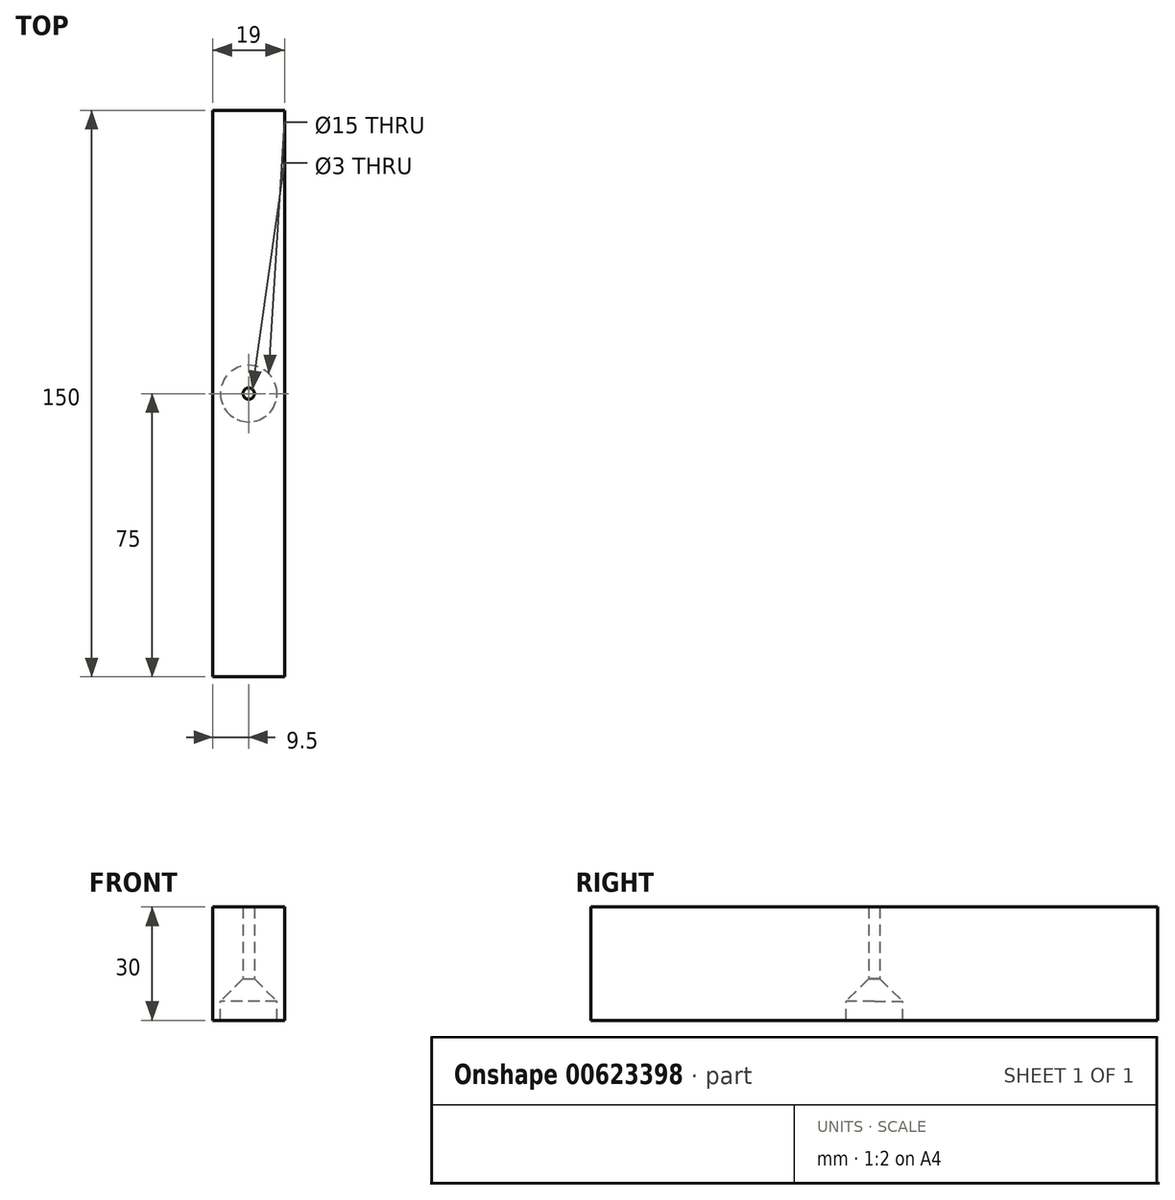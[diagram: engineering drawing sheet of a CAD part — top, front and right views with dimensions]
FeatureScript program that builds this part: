
annotation { "Feature Type Name" : "Feature", "Feature Type Description" : "" }
export const myFeature = defineFeature(function(context is Context, id is Id, definition is map)
    precondition{}
    {
        {
            var Q0;
            Q0=qCreatedBy(makeId("Top.planeOp"),FACE);
            var sketch = newSketch(context, id + "F0", { "sketchPlane" : qUnion([Q0])});
            skLineSegment(sketch, "E0", {"start": v(-50, 0) * mm, "end": v(50, 0) * mm, "construction": true});
            skLineSegment(sketch, "E1", {"start": v(0, 50) * mm, "end": v(0, -50) * mm, "construction": true});
            skSolve(sketch);
        }
        {
            var Q0;
            Q0=qCreatedBy(makeId("Front.planeOp"),FACE);
            var sketch = newSketch(context, id + "F1", { "sketchPlane" : qUnion([Q0])});
            skLineSegment(sketch, "E2.bottom", {"start": v(0, -15) * mm, "end": v(19, -15) * mm});
            skLineSegment(sketch, "E2.top", {"start": v(0, 15) * mm, "end": v(19, 15) * mm});
            skLineSegment(sketch, "E2.left", {"start": v(0, -15) * mm, "end": v(0, 15) * mm});
            skLineSegment(sketch, "E2.right", {"start": v(19, -15) * mm, "end": v(19, 15) * mm});
            skSolve(sketch);
        }
        {
            var Q0;
            Q0=makeQuery(id+"F1.imprint","IMPRINT",FACE,{"disambiguationData":[TD([[makeQuery(id+"F1.imprint","IMPRINT",EDGE,{"derivedFrom":sQuery(id+"F1.wireOp",EDGE,"E2.bottom")}),1.0]])]});
            var Q1;
            Q1 = qConstructionFilter(qBodyType(qCreatedBy(id + "F1" ,EDGE), BodyType.WIRE), ConstructionObject.NO);
            extrude(context, id + "F2", {"entities" : qUnion([Q0]), "surfaceEntities" : qUnion([Q1]), "endBound" : BoundingType.SYMMETRIC, "depth" : 150 * mm, "offsetDistance" : 25 * mm});
        }
        {
            var Q0;
            Q0=makeQuery(id+"F2.opExtrude","SWEPT_FACE",FACE,{"disambiguationData":[OSD([sQuery(id+"F1.wireOp",EDGE,"E2.bottom")])]});
            cPlane(context, id + "F3", {"entities" : qUnion([Q0]), "cplaneType" : CPlaneType.OFFSET, "offset" : 5 * mm, "oppositeDirection" : true, "width" : 150 * mm, "height" : 150 * mm});
        }
        {
            var Q0;
            Q0=qCreatedBy(id+"F3.planeOp",FACE);
            var sketch = newSketch(context, id + "F4", { "sketchPlane" : qUnion([Q0])});
            skPoint(sketch, "E3", {"position": v(9.5, 0) * mm});
            skPoint(sketch, "E3.positionSnap0", {"position": v(19, 0) * mm});
            skPoint(sketch, "E3.positionSnap1", {"position": v(9.5, 75) * mm});
            skCircle(sketch, "E4", {"center": v(9.5, 0) * mm, "radius": 7.5 * mm});
            skSolve(sketch);
        }
        {
            var Q0;
            Q0=makeQuery(id+"F4.imprint","IMPRINT",FACE,{"disambiguationData":[TD([[makeQuery(id+"F4.imprint","IMPRINT",EDGE,{"derivedFrom":sQuery(id+"F4.wireOp",EDGE,"E4")}),1.0]])]});
            var Q1;
            Q1=sQuery(id+"F4.wireOp",EDGE,"E4");
            extrude(context, id + "F5", {"entities" : qUnion([Q0]), "operationType" : NewBodyOperationType.REMOVE, "surfaceEntities" : qUnion([Q1]), "endBound" : BoundingType.UP_TO_NEXT, "depth" : 5 * mm, "offsetDistance" : 25 * mm});
        }
        {
            var Q0;
            Q0=sQuery(id+"F4.wireOp",VERTEX,"E3");
            var Q1;
            Q1=makeQuery(id+"F2.opExtrude","SWEPT_BODY",BODY,{"disambiguationData":[OSD([sQuery(id+"F1.wireOp",EDGE,"E2.bottom"),sQuery(id+"F1.wireOp",EDGE,"E2.top"),sQuery(id+"F1.wireOp",EDGE,"E2.left"),sQuery(id+"F1.wireOp",EDGE,"E2.right")])]});
            hole(context, id + "F6", {"style" : HoleStyle.C_SINK, "endStyle" : HoleEndStyle.THROUGH, "holeDiameter" : 3 * mm, "cSinkDiameter" : 15 * mm, "cSinkAngle" : 90 * degree, "majorDiameter" : 5 * mm, "isTappedThrough" : true, "tappedDepth" : 12 * mm, "tapClearance" : 3, "startFromSketch" : true, "locations" : qUnion([Q0]), "scope" : qUnion([Q1])});
        }
    });
